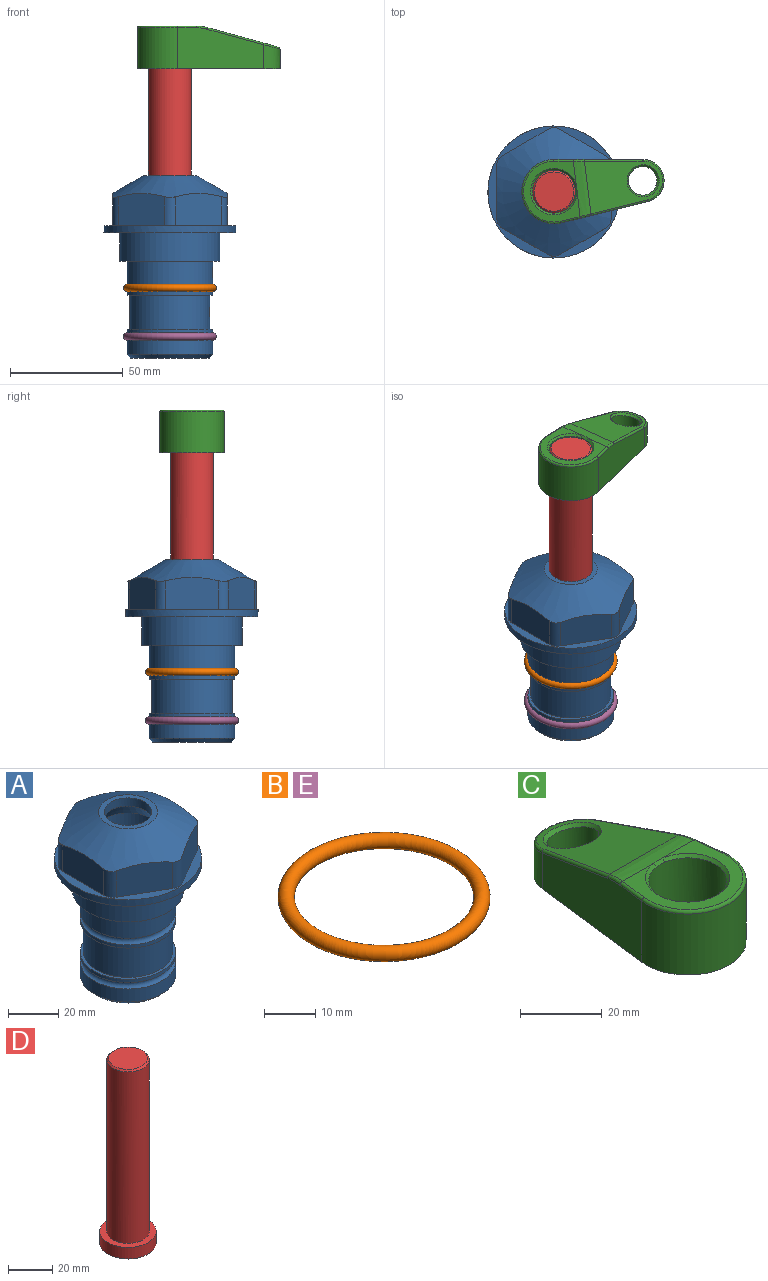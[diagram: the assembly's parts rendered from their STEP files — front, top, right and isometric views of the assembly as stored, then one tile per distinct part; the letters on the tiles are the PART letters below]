
ASSEMBLY  parts=5 mates=4
PART A: 36 faces, bbox 58.7x58.7x81 mm
  f0: cylinder r=17.78mm len=35.56mm, axis (0,0,1), area 1670.8mm2, adj f23,f24,f31
  f1: cylinder r=19.05mm len=38.1mm, axis (0,0,1), area 1191.9mm2, adj f26,f27,f30
  f2: plane 58.66x58.66mm, normal (0,0,-1), area 1150.6mm2, adj f3,f28
  f3: cylinder r=29.33mm len=58.66mm, axis (0,0,-1), area 585.1mm2, adj f2,f4
  f4: plane 58.66x58.66mm, normal (0,0,1), area 475.9mm2, adj f3,f5,f6,f7,f8,f9,f10,f11
  f5: plane 20.32x14.34mm, normal (-0.5,0.87,0), area 324.4mm2, adj f4,f15,f16,f17
  f6: plane 20.32x14.34mm, normal (0.5,0.87,0), area 324.4mm2, adj f4,f14,f15,f17
  f7: plane 23.48x14.34mm, normal (1,0,0), area 324.4mm2, adj f4,f13,f14,f17
  f8: plane 20.32x14.34mm, normal (0.5,-0.87,0), area 324.4mm2, adj f4,f12,f13,f17
  f9: plane 20.32x14.34mm, normal (-0.5,-0.87,0), area 324.4mm2, adj f4,f11,f12,f17
  f10: plane 23.48x14.34mm, normal (-1,0,0), area 324.4mm2, adj f4,f11,f16,f17
  f11: cylinder r=5.08mm len=12.85mm, axis (0,0,-1), area 67.2mm2, adj f4,f9,f10,f17
  f12: cylinder r=5.08mm len=12.85mm, axis (0,0,-1), area 67.2mm2, adj f4,f8,f9,f17
  f13: cylinder r=5.08mm len=12.85mm, axis (0,0,-1), area 67.2mm2, adj f4,f7,f8,f17
  f14: cylinder r=5.08mm len=12.85mm, axis (0,0,-1), area 67.2mm2, adj f4,f6,f7,f17
  f15: cylinder r=5.08mm len=12.85mm, axis (0,0,-1), area 67.2mm2, adj f4,f5,f6,f17
  f16: cylinder r=5.08mm len=12.85mm, axis (0,0,-1), area 67.2mm2, adj f4,f5,f10,f17
  f17: cone r=11.73mm half-angle=60deg, axis (0,0,-1), area 2071.8mm2, adj f5,f6,f7,f8,f9,f10,f11,f12
  f18: plane 23.46x23.46mm, normal (0,0,1), area 147.4mm2, adj f17,f35
  f19: plane 34.93x34.93mm, normal (0,0,-1), area 958mm2, adj f29
  f20: cylinder r=19.05mm len=38.1mm, axis (0,0,1), area 760.1mm2, adj f21,f29
  f21: torus R=19.05mm, axis (0,0,1), area 565.3mm2, adj f20,f22
  f22: cylinder r=19.05mm len=38.1mm, axis (0,0,1), area 190mm2, adj f21,f23
  f23: plane 38.1x38.1mm, normal (0,0,1), area 146.9mm2, adj f0,f22
  f24: plane 38.1x38.1mm, normal (0,0,-1), area 146.9mm2, adj f0,f25
  f25: cylinder r=19.05mm len=38.1mm, axis (0,0,1), area 190mm2, adj f24,f26
  f26: torus R=19.05mm, axis (0,0,1), area 565.3mm2, adj f1,f25
  f27: plane 44.45x44.45mm, normal (0,0,-1), area 411.7mm2, adj f1,f28
  f28: cylinder r=22.23mm len=44.45mm, axis (0,0,1), area 1773.5mm2, adj f2,f27
  f29: cone r=19.05mm half-angle=45deg, axis (0,0,1), area 257.5mm2, adj f19,f20
  f30: cylinder r=3.17mm len=6.75mm, axis (-1,0,0), area 128mm2, adj f1,f33
  f31: cylinder r=3.17mm len=6.35mm, axis (-1,0,0), area 102.5mm2, adj f0,f33
  f32: plane 25.4x25.4mm, normal (0,0,1), area 506.7mm2, adj f33
  f33: cylinder r=12.7mm len=66.42mm, axis (0,0,-1), area 5236.2mm2, adj f30,f31,f32,f34
  f34: cone r=9.53mm half-angle=30deg, axis (0,0,-1), area 443.4mm2, adj f33,f35
  f35: cylinder r=9.53mm len=19.05mm, axis (0,0,-1), area 240.9mm2, adj f18,f34
PART B: 1 faces, bbox 44.7x44.7x3.2 mm
  f0: torus R=19.05mm, axis (0,0,1), area 1193.9mm2
PART C: 31 faces, bbox 31.7x65.5x19.8 mm
  f0: plane 39.12x18.26mm, normal (0.99,0.12,0), area 612.2mm2, adj f1,f4,f7,f11,f13,f15
  f1: cylinder r=9.53mm len=18.91mm, axis (0,0,-1), area 296.1mm2, adj f0,f2,f7,f17
  f2: plane 39.12x18.26mm, normal (-0.99,0.12,0), area 612.2mm2, adj f1,f4,f7,f12,f14,f16
  f3: cylinder r=6.35mm len=12.7mm, axis (0,0,-1), area 362.4mm2, adj f7,f18
  f4: cylinder r=14.29mm len=28.58mm, axis (0,0,-1), area 882.2mm2, adj f0,f2,f7,f10
  f5: cylinder r=9.53mm len=19.05mm, axis (0,0,-1), area 1092.6mm2, adj f7,f19,f20
  f6: plane 26.99x23.69mm, normal (0,0,1), area 216.2mm2, adj f9,f10,f11,f12,f19
  f7: plane 63.5x28.58mm, normal (0,0,-1), area 661.8mm2, adj f0,f1,f2,f3,f4,f5,f22,f23
  f8: plane 33.52x23.6mm, normal (0,0.26,0.97), area 486mm2, adj f9,f15,f16,f17,f18
  f9: cylinder r=19.05mm len=24.72mm, axis (1,0,0), area 120.4mm2, adj f6,f8,f13,f14,f20
  f10: torus R=13.49mm, axis (0,0,1), area 59mm2, adj f4,f6,f11,f12
  f11: cylinder r=0.79mm len=8.67mm, axis (0.12,-0.99,0), area 10.8mm2, adj f0,f6,f10,f13
  f12: cylinder r=0.79mm len=8.67mm, axis (0.12,0.99,0), area 10.8mm2, adj f2,f6,f10,f14
  f13: bspline ~4.95x1.42mm, area 6.1mm2, adj f0,f9,f11,f15
  f14: bspline ~4.95x1.42mm, area 6.1mm2, adj f2,f9,f12,f16
  f15: cylinder r=0.79mm len=25.95mm, axis (0.12,-0.96,0.26), area 32.9mm2, adj f0,f8,f13,f17
  f16: cylinder r=0.79mm len=25.95mm, axis (0.12,0.96,-0.26), area 32.9mm2, adj f2,f8,f14,f17
  f17: bspline ~18.91x8.38mm, area 30mm2, adj f1,f8,f15,f16
  f18: bspline ~14.29x14.29mm, area 48.3mm2, adj f3,f8
  f19: cone r=9.53mm half-angle=45deg, axis (0,0,1), area 66.5mm2, adj f5,f6,f20
  f20: bspline ~3.22x0.96mm, area 3.5mm2, adj f5,f9,f19
  f21: plane 2.75x2.72mm, normal (0,0,-1), area 2.9mm2, adj f23,f25,f28
  f22: plane 23.05x15.88mm, normal (-0.99,-0.12,0), area 323.6mm2, adj f7,f25,f26,f27,f28,f29
  f23: plane 23.05x15.88mm, normal (0.99,-0.12,0), area 323.6mm2, adj f7,f21,f25,f27,f28,f30
  f24: cylinder r=9.53mm len=10.69mm, axis (0,0,-1), area 114.7mm2, adj f7,f27,f29,f30
  f25: cylinder r=12.7mm len=20.59mm, axis (0,0,-1), area 381.1mm2, adj f7,f21,f22,f23,f26,f28
  f26: plane 2.75x2.72mm, normal (0,0,-1), area 2.9mm2, adj f22,f25,f28
  f27: plane 19.72x18.37mm, normal (0,-0.26,-0.97), area 291.8mm2, adj f22,f23,f24,f28,f29,f30
  f28: cylinder r=15.88mm len=19.92mm, axis (1,0,0), area 54.8mm2, adj f21,f22,f23,f25,f26,f27
  f29: cylinder r=1.59mm len=11mm, axis (0,0,-1), area 34.7mm2, adj f7,f22,f24,f27
  f30: cylinder r=1.59mm len=11mm, axis (0,0,-1), area 34.7mm2, adj f7,f23,f24,f27
PART D: 6 faces, bbox 25.4x25.4x101.6 mm
  f0: plane 17.46x17.46mm, normal (0,0,1), area 239.5mm2, adj f5
  f1: plane 25.4x25.4mm, normal (0,0,-1), area 506.7mm2, adj f2
  f2: cylinder r=12.7mm len=25.4mm, axis (0,0,1), area 506.7mm2, adj f1,f3
  f3: plane 25.4x25.4mm, normal (0,0,1), area 221.7mm2, adj f2,f4
  f4: cylinder r=9.53mm len=94.46mm, axis (0,0,1), area 5653mm2, adj f3,f5
  f5: cone r=8.73mm half-angle=45deg, axis (0,0,-1), area 64.4mm2, adj f0,f4
PART E: same geometry as B
PLACE A at identity fixed
PLACE B at identity
PLACE C rot(axis=(0,0,-1),83deg) t=(0,0,28.35)mm
PLACE D rot(axis=(0,0,-1),83deg) t=(0,0,27.55)mm
PLACE E t=(0,0,-21.59)mm
MATE fastened B.f0 <-> A.f0  axis (0,0,1) through (0,0,-24.51)mm
MATE fastened E.f0 <-> A.f0  axis (0,0,1) through (0,0,-46.1)mm
MATE cylindrical A.f0 <-> D.f2  axis (0,0,1) through (0,0,-50.55)mm
MATE fastened C.f4 <-> D.f2  axis (0,0,-1) through (0,0,91.05)mm
